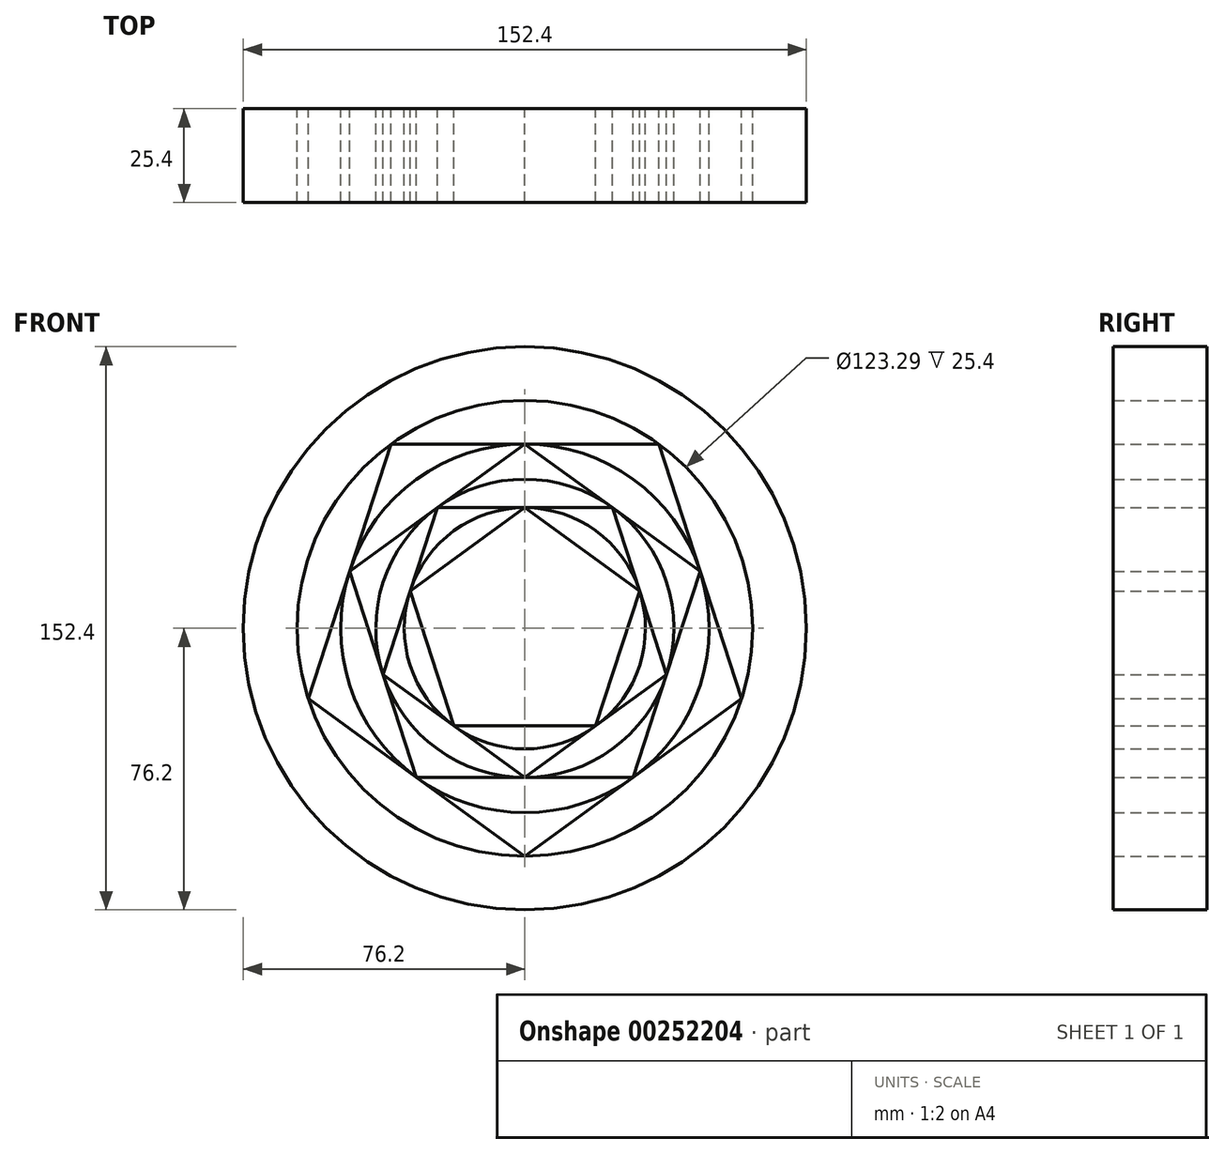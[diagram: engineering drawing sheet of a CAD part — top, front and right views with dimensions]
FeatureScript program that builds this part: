
annotation { "Feature Type Name" : "Feature", "Feature Type Description" : "" }
export const myFeature = defineFeature(function(context is Context, id is Id, definition is map)
    precondition{}
    {
        {
            var Q0;
            Q0=qCreatedBy(makeId("Front.planeOp"),FACE);
            var sketch = newSketch(context, id + "F0", { "sketchPlane" : qUnion([Q0])});
            skCircle(sketch, "E0", {"center": v(0, 0) * mm, "radius": 76.2 * mm});
            skCircle(sketch, "E1.cCircle", {"center": v(0, 0) * mm, "radius": 76.2 * mm, "construction": true});
            skLineSegment(sketch, "E1.0", {"start": v(0, 76.2) * mm, "end": v(72.47, 23.55) * mm});
            skLineSegment(sketch, "E1.1", {"start": v(72.47, 23.55) * mm, "end": v(44.79, -61.65) * mm});
            skLineSegment(sketch, "E1.2", {"start": v(44.79, -61.65) * mm, "end": v(-44.79, -61.65) * mm});
            skLineSegment(sketch, "E1.3", {"start": v(-44.79, -61.65) * mm, "end": v(-72.47, 23.55) * mm});
            skLineSegment(sketch, "E1.4", {"start": v(-72.47, 23.55) * mm, "end": v(0, 76.2) * mm});
            skCircle(sketch, "E2", {"center": v(0, 0) * mm, "radius": 61.65 * mm});
            skCircle(sketch, "E3.cCircle", {"center": v(0, 0) * mm, "radius": 61.65 * mm, "construction": true});
            skLineSegment(sketch, "E3.0", {"start": v(0, -61.65) * mm, "end": v(-58.63, -19.05) * mm});
            skLineSegment(sketch, "E3.1", {"start": v(-58.63, -19.05) * mm, "end": v(-36.24, 49.87) * mm});
            skLineSegment(sketch, "E3.2", {"start": v(-36.24, 49.87) * mm, "end": v(36.24, 49.87) * mm});
            skLineSegment(sketch, "E3.3", {"start": v(36.24, 49.87) * mm, "end": v(58.63, -19.05) * mm});
            skLineSegment(sketch, "E3.4", {"start": v(58.63, -19.05) * mm, "end": v(0, -61.65) * mm});
            skCircle(sketch, "E4", {"center": v(0, 0) * mm, "radius": 49.87 * mm});
            skCircle(sketch, "E5.cCircle", {"center": v(0, 0) * mm, "radius": 49.87 * mm, "construction": true});
            skLineSegment(sketch, "E5.0", {"start": v(0, 49.87) * mm, "end": v(47.43, 15.41) * mm});
            skLineSegment(sketch, "E5.1", {"start": v(47.43, 15.41) * mm, "end": v(29.31, -40.35) * mm});
            skLineSegment(sketch, "E5.2", {"start": v(29.31, -40.35) * mm, "end": v(-29.31, -40.35) * mm});
            skLineSegment(sketch, "E5.3", {"start": v(-29.31, -40.35) * mm, "end": v(-47.43, 15.41) * mm});
            skLineSegment(sketch, "E5.4", {"start": v(-47.43, 15.41) * mm, "end": v(0, 49.87) * mm});
            skCircle(sketch, "E6", {"center": v(0, 0) * mm, "radius": 40.35 * mm});
            skCircle(sketch, "E7.cCircle", {"center": v(0, 0) * mm, "radius": 40.35 * mm, "construction": true});
            skLineSegment(sketch, "E7.0", {"start": v(0, -40.35) * mm, "end": v(-38.37, -12.47) * mm});
            skLineSegment(sketch, "E7.1", {"start": v(-38.37, -12.47) * mm, "end": v(-23.72, 32.64) * mm});
            skLineSegment(sketch, "E7.2", {"start": v(-23.72, 32.64) * mm, "end": v(23.72, 32.64) * mm});
            skLineSegment(sketch, "E7.3", {"start": v(23.72, 32.64) * mm, "end": v(38.37, -12.47) * mm});
            skLineSegment(sketch, "E7.4", {"start": v(38.37, -12.47) * mm, "end": v(0, -40.35) * mm});
            skCircle(sketch, "E8", {"center": v(0, 0) * mm, "radius": 32.64 * mm});
            skCircle(sketch, "E9.cCircle", {"center": v(0, 0) * mm, "radius": 32.64 * mm, "construction": true});
            skLineSegment(sketch, "E9.0", {"start": v(0, 32.64) * mm, "end": v(31.05, 10.09) * mm});
            skLineSegment(sketch, "E9.1", {"start": v(31.05, 10.09) * mm, "end": v(19.19, -26.4) * mm});
            skLineSegment(sketch, "E9.2", {"start": v(19.19, -26.4) * mm, "end": v(-19.19, -26.4) * mm});
            skLineSegment(sketch, "E9.3", {"start": v(-19.19, -26.4) * mm, "end": v(-31.05, 10.09) * mm});
            skLineSegment(sketch, "E9.4", {"start": v(-31.05, 10.09) * mm, "end": v(0, 32.64) * mm});
            skSolve(sketch);
        }
        {
            var Q0;
            Q0 = qSketchRegion(id + "F0", true);
            var Q1;
            Q1=makeQuery(id+"F0.imprint","IMPRINT",FACE,{"disambiguationData":[TD([[makeQuery(id+"F0.imprint","IMPRINT",EDGE,{"derivedFrom":sQuery(id+"F0.wireOp",EDGE,"E9.0")}),-1.0]])]});
            var Q2;
            {var subQ0=sQuery(id+"F0.wireOp",EDGE,"E7.1");var subQ1=sQuery(id+"F0.wireOp",EDGE,"E7.0");var subQ2=makeQuery(id+"F0.imprint","INTERSECT",VERTEX,{"derivedFrom":[sQuery(id+"F0.wireOp",EDGE,"E5.3"),sQuery(id+"F0.wireOp",EDGE,"E6"),subQ1,subQ0]});Q2=makeQuery(id+"F0.imprint","IMPRINT",FACE,{"disambiguationData":[TD([[makeQuery(id+"F0.imprint","IMPRINT",EDGE,{"disambiguationData":[TD([[subQ2,1.0]])],"derivedFrom":subQ1}),-1.0]])]});}
            var Q3;
            {var subQ0=sQuery(id+"F0.wireOp",EDGE,"E7.4");var subQ1=sQuery(id+"F0.wireOp",EDGE,"E7.0");var subQ2=makeQuery(id+"F0.imprint","INTERSECT",VERTEX,{"derivedFrom":[sQuery(id+"F0.wireOp",EDGE,"E5.2"),sQuery(id+"F0.wireOp",EDGE,"E6"),subQ1,subQ0]});Q3=makeQuery(id+"F0.imprint","IMPRINT",FACE,{"disambiguationData":[TD([[makeQuery(id+"F0.imprint","IMPRINT",EDGE,{"disambiguationData":[TD([[subQ2,-1.0]])],"derivedFrom":subQ1}),-1.0]])]});}
            var Q4;
            {var subQ0=sQuery(id+"F0.wireOp",EDGE,"E7.4");var subQ1=sQuery(id+"F0.wireOp",EDGE,"E7.3");var subQ2=makeQuery(id+"F0.imprint","INTERSECT",VERTEX,{"derivedFrom":[sQuery(id+"F0.wireOp",EDGE,"E5.1"),sQuery(id+"F0.wireOp",EDGE,"E6"),subQ1,subQ0]});Q4=makeQuery(id+"F0.imprint","IMPRINT",FACE,{"disambiguationData":[TD([[makeQuery(id+"F0.imprint","IMPRINT",EDGE,{"disambiguationData":[TD([[subQ2,1.0]])],"derivedFrom":subQ1}),-1.0]])]});}
            var Q5;
            {var subQ0=sQuery(id+"F0.wireOp",EDGE,"E7.3");var subQ1=sQuery(id+"F0.wireOp",EDGE,"E7.2");var subQ2=makeQuery(id+"F0.imprint","INTERSECT",VERTEX,{"derivedFrom":[sQuery(id+"F0.wireOp",EDGE,"E5.0"),sQuery(id+"F0.wireOp",EDGE,"E6"),subQ1,subQ0]});Q5=makeQuery(id+"F0.imprint","IMPRINT",FACE,{"disambiguationData":[TD([[makeQuery(id+"F0.imprint","IMPRINT",EDGE,{"disambiguationData":[TD([[subQ2,1.0]])],"derivedFrom":subQ1}),-1.0]])]});}
            var Q6;
            {var subQ0=sQuery(id+"F0.wireOp",EDGE,"E7.2");var subQ1=sQuery(id+"F0.wireOp",EDGE,"E7.1");var subQ2=makeQuery(id+"F0.imprint","INTERSECT",VERTEX,{"derivedFrom":[sQuery(id+"F0.wireOp",EDGE,"E5.4"),sQuery(id+"F0.wireOp",EDGE,"E6"),subQ1,subQ0]});Q6=makeQuery(id+"F0.imprint","IMPRINT",FACE,{"disambiguationData":[TD([[makeQuery(id+"F0.imprint","IMPRINT",EDGE,{"disambiguationData":[TD([[subQ2,1.0]])],"derivedFrom":subQ1}),-1.0]])]});}
            var Q7;
            {var subQ0=sQuery(id+"F0.wireOp",EDGE,"E5.4");var subQ1=sQuery(id+"F0.wireOp",EDGE,"E5.3");var subQ2=makeQuery(id+"F0.imprint","INTERSECT",VERTEX,{"derivedFrom":[sQuery(id+"F0.wireOp",EDGE,"E3.1"),sQuery(id+"F0.wireOp",EDGE,"E4"),subQ1,subQ0]});Q7=makeQuery(id+"F0.imprint","IMPRINT",FACE,{"disambiguationData":[TD([[makeQuery(id+"F0.imprint","IMPRINT",EDGE,{"disambiguationData":[TD([[subQ2,1.0]])],"derivedFrom":subQ1}),-1.0]])]});}
            var Q8;
            {var subQ0=sQuery(id+"F0.wireOp",EDGE,"E5.3");var subQ1=sQuery(id+"F0.wireOp",EDGE,"E5.2");var subQ2=makeQuery(id+"F0.imprint","INTERSECT",VERTEX,{"derivedFrom":[sQuery(id+"F0.wireOp",EDGE,"E3.0"),sQuery(id+"F0.wireOp",EDGE,"E4"),subQ1,subQ0]});Q8=makeQuery(id+"F0.imprint","IMPRINT",FACE,{"disambiguationData":[TD([[makeQuery(id+"F0.imprint","IMPRINT",EDGE,{"disambiguationData":[TD([[subQ2,1.0]])],"derivedFrom":subQ1}),-1.0]])]});}
            var Q9;
            {var subQ0=sQuery(id+"F0.wireOp",EDGE,"E5.2");var subQ1=sQuery(id+"F0.wireOp",EDGE,"E5.1");var subQ2=makeQuery(id+"F0.imprint","INTERSECT",VERTEX,{"derivedFrom":[sQuery(id+"F0.wireOp",EDGE,"E3.4"),sQuery(id+"F0.wireOp",EDGE,"E4"),subQ1,subQ0]});Q9=makeQuery(id+"F0.imprint","IMPRINT",FACE,{"disambiguationData":[TD([[makeQuery(id+"F0.imprint","IMPRINT",EDGE,{"disambiguationData":[TD([[subQ2,1.0]])],"derivedFrom":subQ1}),-1.0]])]});}
            var Q10;
            {var subQ0=sQuery(id+"F0.wireOp",EDGE,"E5.1");var subQ1=sQuery(id+"F0.wireOp",EDGE,"E5.0");var subQ2=makeQuery(id+"F0.imprint","INTERSECT",VERTEX,{"derivedFrom":[sQuery(id+"F0.wireOp",EDGE,"E3.3"),sQuery(id+"F0.wireOp",EDGE,"E4"),subQ1,subQ0]});Q10=makeQuery(id+"F0.imprint","IMPRINT",FACE,{"disambiguationData":[TD([[makeQuery(id+"F0.imprint","IMPRINT",EDGE,{"disambiguationData":[TD([[subQ2,1.0]])],"derivedFrom":subQ1}),-1.0]])]});}
            var Q11;
            {var subQ0=sQuery(id+"F0.wireOp",EDGE,"E5.4");var subQ1=sQuery(id+"F0.wireOp",EDGE,"E5.0");var subQ2=makeQuery(id+"F0.imprint","INTERSECT",VERTEX,{"derivedFrom":[sQuery(id+"F0.wireOp",EDGE,"E3.2"),sQuery(id+"F0.wireOp",EDGE,"E4"),subQ1,subQ0]});Q11=makeQuery(id+"F0.imprint","IMPRINT",FACE,{"disambiguationData":[TD([[makeQuery(id+"F0.imprint","IMPRINT",EDGE,{"disambiguationData":[TD([[subQ2,-1.0]])],"derivedFrom":subQ1}),-1.0]])]});}
            var Q12;
            {var subQ0=sQuery(id+"F0.wireOp",EDGE,"E3.2");var subQ1=sQuery(id+"F0.wireOp",EDGE,"E3.1");var subQ2=makeQuery(id+"F0.imprint","INTERSECT",VERTEX,{"derivedFrom":[sQuery(id+"F0.wireOp",EDGE,"E1.4"),sQuery(id+"F0.wireOp",EDGE,"E2"),subQ1,subQ0]});Q12=makeQuery(id+"F0.imprint","IMPRINT",FACE,{"disambiguationData":[TD([[makeQuery(id+"F0.imprint","IMPRINT",EDGE,{"disambiguationData":[TD([[subQ2,1.0]])],"derivedFrom":subQ1}),-1.0]])]});}
            var Q13;
            {var subQ0=sQuery(id+"F0.wireOp",EDGE,"E3.1");var subQ1=sQuery(id+"F0.wireOp",EDGE,"E3.0");var subQ2=makeQuery(id+"F0.imprint","INTERSECT",VERTEX,{"derivedFrom":[sQuery(id+"F0.wireOp",EDGE,"E1.3"),sQuery(id+"F0.wireOp",EDGE,"E2"),subQ1,subQ0]});Q13=makeQuery(id+"F0.imprint","IMPRINT",FACE,{"disambiguationData":[TD([[makeQuery(id+"F0.imprint","IMPRINT",EDGE,{"disambiguationData":[TD([[subQ2,1.0]])],"derivedFrom":subQ1}),-1.0]])]});}
            var Q14;
            {var subQ0=sQuery(id+"F0.wireOp",EDGE,"E3.4");var subQ1=sQuery(id+"F0.wireOp",EDGE,"E3.0");var subQ2=makeQuery(id+"F0.imprint","INTERSECT",VERTEX,{"derivedFrom":[sQuery(id+"F0.wireOp",EDGE,"E1.2"),sQuery(id+"F0.wireOp",EDGE,"E2"),subQ1,subQ0]});Q14=makeQuery(id+"F0.imprint","IMPRINT",FACE,{"disambiguationData":[TD([[makeQuery(id+"F0.imprint","IMPRINT",EDGE,{"disambiguationData":[TD([[subQ2,-1.0]])],"derivedFrom":subQ1}),-1.0]])]});}
            var Q15;
            {var subQ0=sQuery(id+"F0.wireOp",EDGE,"E3.4");var subQ1=sQuery(id+"F0.wireOp",EDGE,"E3.3");var subQ2=makeQuery(id+"F0.imprint","INTERSECT",VERTEX,{"derivedFrom":[sQuery(id+"F0.wireOp",EDGE,"E1.1"),sQuery(id+"F0.wireOp",EDGE,"E2"),subQ1,subQ0]});Q15=makeQuery(id+"F0.imprint","IMPRINT",FACE,{"disambiguationData":[TD([[makeQuery(id+"F0.imprint","IMPRINT",EDGE,{"disambiguationData":[TD([[subQ2,1.0]])],"derivedFrom":subQ1}),-1.0]])]});}
            var Q16;
            {var subQ0=sQuery(id+"F0.wireOp",EDGE,"E3.3");var subQ1=sQuery(id+"F0.wireOp",EDGE,"E3.2");var subQ2=makeQuery(id+"F0.imprint","INTERSECT",VERTEX,{"derivedFrom":[sQuery(id+"F0.wireOp",EDGE,"E1.0"),sQuery(id+"F0.wireOp",EDGE,"E2"),subQ1,subQ0]});Q16=makeQuery(id+"F0.imprint","IMPRINT",FACE,{"disambiguationData":[TD([[makeQuery(id+"F0.imprint","IMPRINT",EDGE,{"disambiguationData":[TD([[subQ2,1.0]])],"derivedFrom":subQ1}),-1.0]])]});}
            extrude(context, id + "F1", {"entities" : qUnion([Q0, Q1, Q2, Q3, Q4, Q5, Q6, Q7, Q8, Q9, Q10, Q11, Q12, Q13, Q14, Q15, Q16]), "depth" : 25.4 * mm});
        }
    });
